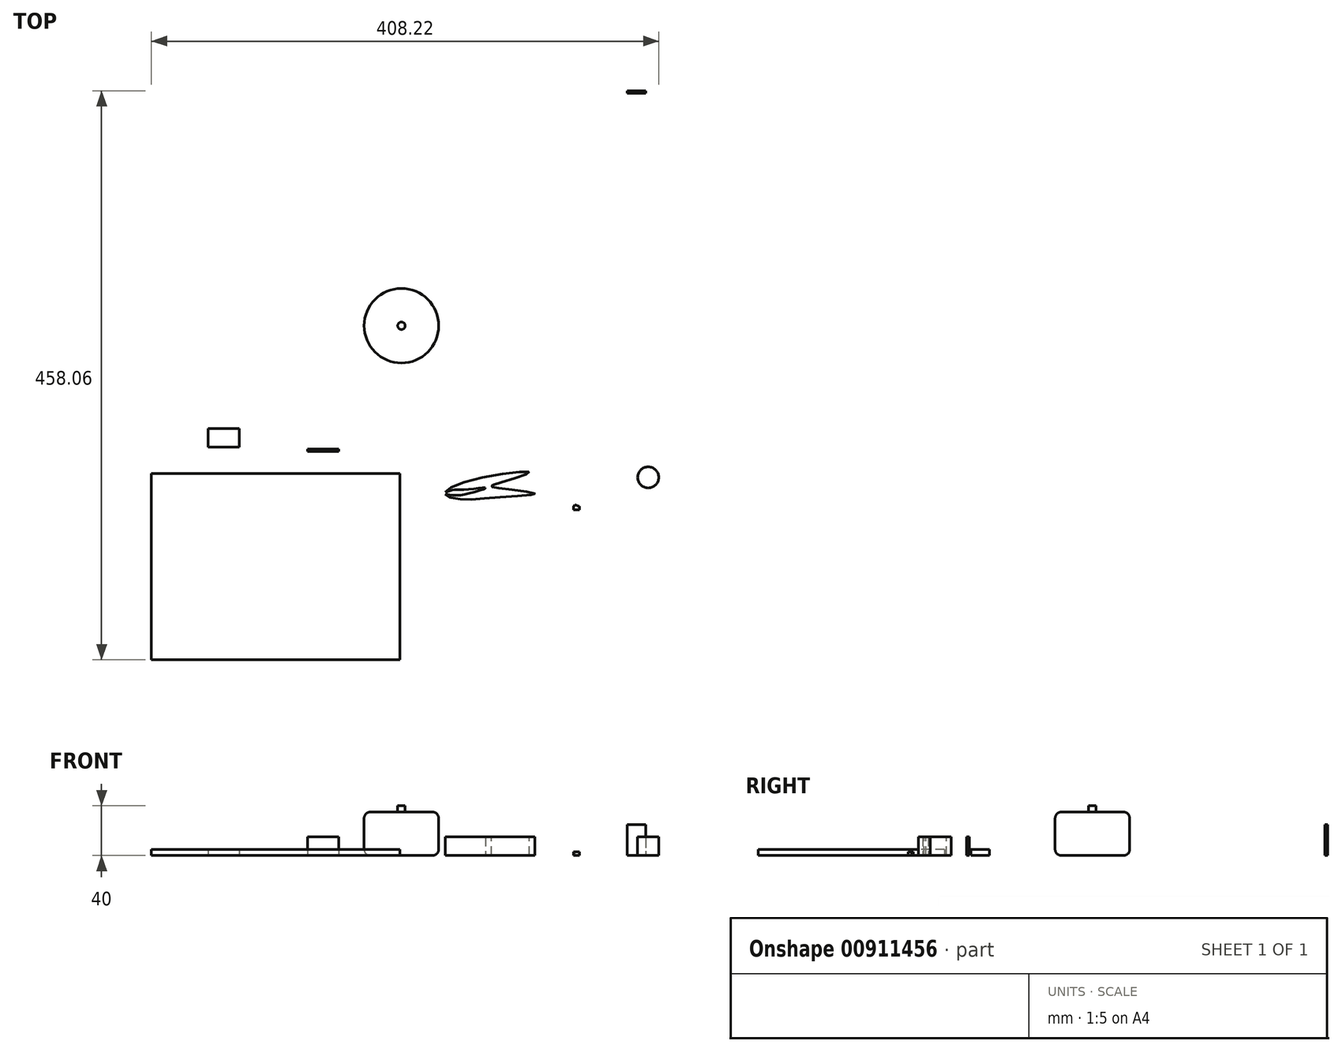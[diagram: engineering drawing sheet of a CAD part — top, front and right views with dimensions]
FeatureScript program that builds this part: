
annotation { "Feature Type Name" : "Feature", "Feature Type Description" : "" }
export const myFeature = defineFeature(function(context is Context, id is Id, definition is map)
    precondition{}
    {
        {
            var Q0;
            Q0=qCreatedBy(makeId("Top.planeOp"),FACE);
            var sketch = newSketch(context, id + "F0", { "sketchPlane" : qUnion([Q0])});
            skLineSegment(sketch, "E0.bottom", {"start": v(-321.83, 125.98) * mm, "end": v(-121.83, 125.98) * mm});
            skLineSegment(sketch, "E0.top", {"start": v(-321.83, -24.02) * mm, "end": v(-121.83, -24.02) * mm});
            skLineSegment(sketch, "E0.left", {"start": v(-321.83, 125.98) * mm, "end": v(-321.83, -24.02) * mm});
            skLineSegment(sketch, "E0.right", {"start": v(-121.83, 125.98) * mm, "end": v(-121.83, -24.02) * mm});
            skSolve(sketch);
        }
        {
            var Q0;
            Q0=makeQuery(id+"F0.imprint","IMPRINT",FACE,{"disambiguationData":[TD([[makeQuery(id+"F0.imprint","IMPRINT",EDGE,{"derivedFrom":sQuery(id+"F0.wireOp",EDGE,"E0.bottom")}),-1.0]])]});
            extrude(context, id + "F1", {"entities" : qUnion([Q0]), "depth" : 5 * mm, "offsetDistance" : 25 * mm});
        }
        {
            var Q0;
            Q0=qCreatedBy(makeId("Top.planeOp"),FACE);
            var sketch = newSketch(context, id + "F2", { "sketchPlane" : qUnion([Q0])});
            skCircle(sketch, "E1", {"center": v(-120.67, 244.88) * mm, "radius": 30 * mm});
            skSolve(sketch);
        }
        {
            var Q0;
            Q0=makeQuery(id+"F2.imprint","IMPRINT",FACE,{"disambiguationData":[TD([[makeQuery(id+"F2.imprint","IMPRINT",EDGE,{"derivedFrom":sQuery(id+"F2.wireOp",EDGE,"E1")}),1.0]])]});
            extrude(context, id + "F3", {"entities" : qUnion([Q0]), "depth" : 35 * mm, "offsetDistance" : 25 * mm});
        }
        {
            var Q0;
            Q0=makeQuery(id+"F3.opExtrude","CAP_FACE",FACE,{"disambiguationData":[OSD([sQuery(id+"F2.wireOp",EDGE,"E1")])],"isStart":false});
            var Q1;
            Q1=makeQuery(id+"F3.opExtrude","SWEPT_FACE",FACE,{"disambiguationData":[OSD([sQuery(id+"F2.wireOp",EDGE,"E1")])]});
            fillet(context, id + "F4", {"entities" : qUnion([Q0, Q1]), "radius" : 5 * mm, "tangentPropagation" : true, "allowEdgeOverflow" : false});
        }
        {
            var Q0;
            Q0=makeQuery(id+"F3.opExtrude","CAP_FACE",FACE,{"disambiguationData":[OSD([sQuery(id+"F2.wireOp",EDGE,"E1")])],"isStart":false});
            var sketch = newSketch(context, id + "F5", { "sketchPlane" : qUnion([Q0])});
            skCircle(sketch, "E2", {"center": v(-120.67, 244.88) * mm, "radius": 3 * mm});
            skSolve(sketch);
        }
        {
            var Q0;
            Q0=makeQuery(id+"F5.imprint","IMPRINT",FACE,{"disambiguationData":[TD([[makeQuery(id+"F5.imprint","IMPRINT",EDGE,{"derivedFrom":sQuery(id+"F5.wireOp",EDGE,"E2")}),1.0]])]});
            extrude(context, id + "F6", {"entities" : qUnion([Q0]), "operationType" : NewBodyOperationType.ADD, "depth" : 5 * mm, "offsetDistance" : 25 * mm});
        }
        {
            var Q0;
            Q0=qCreatedBy(makeId("Top.planeOp"),FACE);
            var sketch = newSketch(context, id + "F7", { "sketchPlane" : qUnion([Q0])});
            skLineSegment(sketch, "E3.bottom", {"start": v(-276.1, 162.13) * mm, "end": v(-251.1, 162.13) * mm});
            skLineSegment(sketch, "E3.top", {"start": v(-276.1, 147.13) * mm, "end": v(-251.1, 147.13) * mm});
            skLineSegment(sketch, "E3.left", {"start": v(-276.1, 162.13) * mm, "end": v(-276.1, 147.13) * mm});
            skLineSegment(sketch, "E3.right", {"start": v(-251.1, 162.13) * mm, "end": v(-251.1, 147.13) * mm});
            skSolve(sketch);
        }
        {
            var Q0;
            Q0=makeQuery(id+"F7.imprint","IMPRINT",FACE,{"disambiguationData":[TD([[makeQuery(id+"F7.imprint","IMPRINT",EDGE,{"derivedFrom":sQuery(id+"F7.wireOp",EDGE,"E3.bottom")}),-1.0]])]});
            extrude(context, id + "F8", {"entities" : qUnion([Q0]), "depth" : 5 * mm, "offsetDistance" : 25 * mm});
        }
        {
            var Q0;
            Q0=qCreatedBy(makeId("Top.planeOp"),FACE);
            var sketch = newSketch(context, id + "F9", { "sketchPlane" : qUnion([Q0])});
            skFitSpline(sketch, "E4", {"points": [v(-45.33, 106.5) * mm, v(-76.45, 105.55) * mm, v(-85.66, 110) * mm, v(-61.53, 121.43) * mm, v(-17.71, 126.82) * mm, v(-39.94, 118.89) * mm, v(-48.2, 115.71) * mm, v(-39.94, 113.8) * mm, v(-13.27, 109.68) * mm, v(-45.33, 106.5) * mm]});
            skSolve(sketch);
        }
        {
            var Q0;
            Q0=makeQuery(id+"F9.imprint","IMPRINT",FACE,{"disambiguationData":[TD([[makeQuery(id+"F9.imprint","IMPRINT",EDGE,{"derivedFrom":sQuery(id+"F9.wireOp",EDGE,"E4")}),-1.0]])]});
            extrude(context, id + "F10", {"entities" : qUnion([Q0]), "depth" : 15 * mm, "offsetDistance" : 25 * mm});
        }
        {
            var Q0;
            Q0=makeQuery(id+"F10.opExtrude","CAP_FACE",FACE,{"disambiguationData":[OSD([sQuery(id+"F9.wireOp",EDGE,"E4")])],"isStart":false});
            var sketch = newSketch(context, id + "F11", { "sketchPlane" : qUnion([Q0])});
            skFitSpline(sketch, "E5", {"points": [v(-85.5, 110.95) * mm, v(-79.68, 112.61) * mm, v(-69.33, 112.88) * mm, v(-53.11, 114.42) * mm, v(-68.87, 109.28) * mm, v(-85.48, 109.41) * mm], "startDerivative": vector(43.02, 2.65) * mm, "endDerivative": vector(-84.42, 17.32) * mm});
            skSolve(sketch);
        }
        {
            var Q0;
            {var subQ0=sQuery(id+"F11.wireOp",EDGE,"E5");Q0=makeQuery(id+"F11.imprint","IMPRINT",FACE,{"disambiguationData":[TD([[makeQuery(id+"F11.imprint","IMPRINT",EDGE,{"derivedFrom":subQ0}),-1.0]])]});}
            extrude(context, id + "F12", {"entities" : qUnion([Q0]), "operationType" : NewBodyOperationType.REMOVE, "oppositeDirection" : true, "depth" : 15 * mm, "offsetDistance" : 25 * mm});
        }
        {
            var Q0;
            Q0=qCreatedBy(makeId("Top.planeOp"),FACE);
            var sketch = newSketch(context, id + "F13", { "sketchPlane" : qUnion([Q0])});
            skCircle(sketch, "E6", {"center": v(77.9, 122.82) * mm, "radius": 8.5 * mm});
            skSolve(sketch);
        }
        {
            var Q0;
            Q0=makeQuery(id+"F13.imprint","IMPRINT",FACE,{"disambiguationData":[TD([[makeQuery(id+"F13.imprint","IMPRINT",EDGE,{"derivedFrom":sQuery(id+"F13.wireOp",EDGE,"E6")}),1.0]])]});
            var Q1;
            Q1=sQuery(id+"F13.wireOp",EDGE,"E6");
            extrude(context, id + "F14", {"entities" : qUnion([Q0]), "surfaceEntities" : qUnion([Q1]), "depth" : 15 * mm, "offsetDistance" : 25 * mm});
        }
        {
            var Q0;
            Q0=qCreatedBy(makeId("Top.planeOp"),FACE);
            var sketch = newSketch(context, id + "F15", { "sketchPlane" : qUnion([Q0])});
            skLineSegment(sketch, "E7.bottom", {"start": v(22.69, 96.58) * mm, "end": v(17.69, 96.58) * mm});
            skLineSegment(sketch, "E7.top", {"start": v(22.69, 99.58) * mm, "end": v(17.69, 99.58) * mm});
            skLineSegment(sketch, "E7.left", {"start": v(22.69, 96.58) * mm, "end": v(22.69, 99.58) * mm});
            skLineSegment(sketch, "E7.right", {"start": v(17.69, 96.58) * mm, "end": v(17.69, 99.58) * mm});
            skPoint(sketch, "E7.middle", {"position": v(20.19, 98.08) * mm});
            skLineSegment(sketch, "E8", {"start": v(17.97, 99.58) * mm, "end": v(18.9, 100.75) * mm});
            skLineSegment(sketch, "E9", {"start": v(18.9, 100.75) * mm, "end": v(22.2, 99.58) * mm});
            skSolve(sketch);
        }
        {
            var Q0;
            Q0=makeQuery(id+"F15.imprint","IMPRINT",FACE,{"disambiguationData":[TD([[makeQuery(id+"F15.imprint","IMPRINT",EDGE,{"derivedFrom":sQuery(id+"F15.wireOp",EDGE,"E7.bottom")}),-1.0]])]});
            var Q1;
            {var subQ0=sQuery(id+"F15.wireOp",EDGE,"E8");Q1=makeQuery(id+"F15.imprint","IMPRINT",FACE,{"disambiguationData":[TD([[makeQuery(id+"F15.imprint","IMPRINT",EDGE,{"derivedFrom":subQ0}),-1.0]])]});}
            extrude(context, id + "F16", {"entities" : qUnion([Q0, Q1]), "depth" : 3 * mm, "offsetDistance" : 25 * mm});
        }
        {
            var Q0;
            Q0=qCreatedBy(makeId("Top.planeOp"),FACE);
            var sketch = newSketch(context, id + "F17", { "sketchPlane" : qUnion([Q0])});
            skLineSegment(sketch, "E10.bottom", {"start": v(-171.15, 143.72) * mm, "end": v(-196.15, 143.72) * mm});
            skLineSegment(sketch, "E10.top", {"start": v(-171.15, 145.72) * mm, "end": v(-196.15, 145.72) * mm});
            skLineSegment(sketch, "E10.left", {"start": v(-171.15, 143.72) * mm, "end": v(-171.15, 145.72) * mm});
            skLineSegment(sketch, "E10.right", {"start": v(-196.15, 143.72) * mm, "end": v(-196.15, 145.72) * mm});
            skPoint(sketch, "E10.middle", {"position": v(-183.65, 144.72) * mm});
            skSolve(sketch);
        }
        {
            var Q0;
            Q0=makeQuery(id+"F17.imprint","IMPRINT",FACE,{"disambiguationData":[TD([[makeQuery(id+"F17.imprint","IMPRINT",EDGE,{"derivedFrom":sQuery(id+"F17.wireOp",EDGE,"E10.bottom")}),-1.0]])]});
            extrude(context, id + "F18", {"entities" : qUnion([Q0]), "depth" : 15 * mm, "offsetDistance" : 25 * mm});
        }
        {
            var Q0;
            Q0=qCreatedBy(makeId("Top.planeOp"),FACE);
            var sketch = newSketch(context, id + "F19", { "sketchPlane" : qUnion([Q0])});
            skLineSegment(sketch, "E11.bottom", {"start": v(75.88, 432.04) * mm, "end": v(60.88, 432.04) * mm});
            skLineSegment(sketch, "E11.top", {"start": v(75.88, 434.04) * mm, "end": v(60.88, 434.04) * mm});
            skLineSegment(sketch, "E11.left", {"start": v(75.88, 432.04) * mm, "end": v(75.88, 434.04) * mm});
            skLineSegment(sketch, "E11.right", {"start": v(60.88, 432.04) * mm, "end": v(60.88, 434.04) * mm});
            skPoint(sketch, "E11.middle", {"position": v(68.38, 433.04) * mm});
            skSolve(sketch);
        }
        {
            var Q0;
            Q0=makeQuery(id+"F19.imprint","IMPRINT",FACE,{"disambiguationData":[TD([[makeQuery(id+"F19.imprint","IMPRINT",EDGE,{"derivedFrom":sQuery(id+"F19.wireOp",EDGE,"E11.bottom")}),-1.0]])]});
            extrude(context, id + "F20", {"entities" : qUnion([Q0]), "depth" : 25 * mm, "offsetDistance" : 25 * mm});
        }
    });
